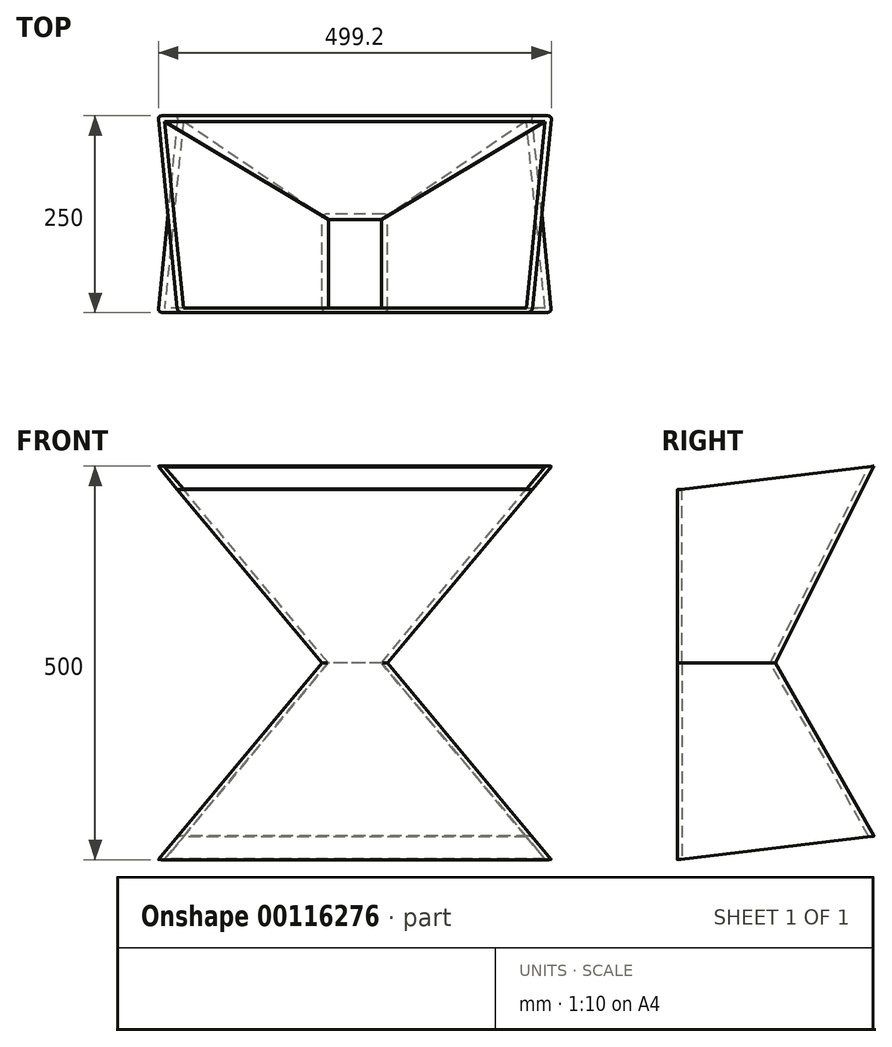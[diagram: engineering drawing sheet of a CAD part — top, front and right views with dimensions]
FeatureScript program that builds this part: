
annotation { "Feature Type Name" : "Feature", "Feature Type Description" : "" }
export const myFeature = defineFeature(function(context is Context, id is Id, definition is map)
    precondition{}
    {
        {
            var Q0;
            Q0=qCreatedBy(makeId("Front.planeOp"),FACE);
            var sketch = newSketch(context, id + "F0", { "sketchPlane" : qUnion([Q0])});
            skLineSegment(sketch, "E0.bottom", {"start": v(250, -250) * mm, "end": v(-250, -250) * mm});
            skLineSegment(sketch, "E0.top", {"start": v(250, 250) * mm, "end": v(-250, 250) * mm});
            skPoint(sketch, "E0.middle", {"position": v(0, 0) * mm});
            skLineSegment(sketch, "E1", {"start": v(-41.48, 0) * mm, "end": v(-250, 250) * mm});
            skLineSegment(sketch, "E2.MirrorCS", {"start": v(41.48, 0) * mm, "end": v(250, 250) * mm});
            skPoint(sketch, "E3.MirrorCS.end.orphan", {"position": v(41.48, 0) * mm});
            skLineSegment(sketch, "E4", {"start": v(-41.48, 0) * mm, "end": v(-250, -250) * mm});
            skLineSegment(sketch, "E5", {"start": v(41.48, 0) * mm, "end": v(250, -250) * mm});
            skSolve(sketch);
        }
        {
            var Q0;
            Q0 = qSketchRegion(id + "F0", true);
            extrude(context, id + "F1", {"entities" : qUnion([Q0]), "endBound" : BoundingType.SYMMETRIC, "depth" : 250 * mm});
        }
        {
            var Q0;
            Q0=makeQuery(id+"F1.opExtrude","CAP_EDGE",EDGE,{"disambiguationData":[OSD([sQuery(id+"F0.wireOp",EDGE,"E0.bottom")])],"isStart":true});
            var Q1;
            Q1=makeQuery(id+"F1.opExtrude","CAP_EDGE",EDGE,{"disambiguationData":[OSD([sQuery(id+"F0.wireOp",EDGE,"E0.top")])],"isStart":false});
            chamfer(context, id + "F2", {"entities" : qUnion([Q0, Q1]), "chamferType" : ChamferType.TWO_OFFSETS, "width1" : 30 * mm, "oppositeDirection" : false, "width2" : 250 * mm, "tangentPropagation" : true});
        }
        {
            var Q0;
            Q0=qCreatedBy(makeId("Right.planeOp"),FACE);
            var sketch = newSketch(context, id + "F3", { "sketchPlane" : qUnion([Q0])});
            skLineSegment(sketch, "E6.0", {"start": v(125, 0) * mm, "end": v(125, -220) * mm});
            skLineSegment(sketch, "E7.0", {"start": v(125, 0) * mm, "end": v(125, 250) * mm});
            skLineSegment(sketch, "E8", {"start": v(0, 0) * mm, "end": v(125, -220) * mm});
            skLineSegment(sketch, "E9", {"start": v(0, 0) * mm, "end": v(125, 250) * mm});
            skPoint(sketch, "E10.0.end.orphan", {"position": v(-125, 220) * mm});
            skPoint(sketch, "E11.0.start.orphan", {"position": v(-125, -250) * mm});
            skPoint(sketch, "E12.orphan", {"position": v(-125, 0) * mm});
            skSolve(sketch);
        }
        {
            var Q0;
            Q0 = qSketchRegion(id + "F3", true);
            extrude(context, id + "F4", {"entities" : qUnion([Q0]), "operationType" : NewBodyOperationType.REMOVE, "endBound" : BoundingType.SYMMETRIC, "depth" : 500 * mm});
        }
        {
            var Q0;
            Q0=makeQuery(id+"F2.opChamfer","BLEND_FACE",FACE,{"disambiguationData":[OSD([sQuery(id+"F0.wireOp",EDGE,"E0.bottom")])]});
            var Q1;
            Q1=makeQuery(id+"F2.opChamfer","BLEND_FACE",FACE,{"disambiguationData":[OSD([sQuery(id+"F0.wireOp",EDGE,"E0.top")])]});
            shell(context, id + "F5", {"entities" : qUnion([Q0, Q1]), "thickness" : 6 * mm});
        }
        {
            var Q0;
            Q0=makeQuery(id+"F1.opExtrude","CAP_EDGE",EDGE,{"disambiguationData":[OSD([sQuery(id+"F0.wireOp",EDGE,"E1")])],"isStart":false});
            var Q1;
            Q1=makeQuery(id+"F1.opExtrude","CAP_EDGE",EDGE,{"disambiguationData":[OSD([sQuery(id+"F0.wireOp",EDGE,"E2.MirrorCS")])],"isStart":false});
            var Q2;
            Q2=makeQuery(id+"F4.boolean.opBoolean","INTERSECT",EDGE,{"derivedFrom":[makeQuery(id+"F1.opExtrude","SWEPT_FACE",FACE,{"disambiguationData":[OSD([sQuery(id+"F0.wireOp",EDGE,"E2.MirrorCS")])]}),makeQuery(id+"F4.opExtrude","SWEPT_FACE",FACE,{"disambiguationData":[OSD([sQuery(id+"F3.wireOp",EDGE,"E9")])]})]});
            var Q3;
            Q3=makeQuery(id+"F4.boolean.opBoolean","INTERSECT",EDGE,{"derivedFrom":[makeQuery(id+"F1.opExtrude","SWEPT_FACE",FACE,{"disambiguationData":[OSD([sQuery(id+"F0.wireOp",EDGE,"E5")])]}),makeQuery(id+"F4.opExtrude","SWEPT_FACE",FACE,{"disambiguationData":[OSD([sQuery(id+"F3.wireOp",EDGE,"E8")])]})]});
            var Q4;
            Q4=makeQuery(id+"F1.opExtrude","CAP_EDGE",EDGE,{"disambiguationData":[OSD([sQuery(id+"F0.wireOp",EDGE,"E5")])],"isStart":false});
            var Q5;
            Q5=makeQuery(id+"F1.opExtrude","CAP_EDGE",EDGE,{"disambiguationData":[OSD([sQuery(id+"F0.wireOp",EDGE,"E4")])],"isStart":false});
            var Q6;
            Q6=makeQuery(id+"F4.boolean.opBoolean","INTERSECT",EDGE,{"derivedFrom":[makeQuery(id+"F1.opExtrude","SWEPT_FACE",FACE,{"disambiguationData":[OSD([sQuery(id+"F0.wireOp",EDGE,"E4")])]}),makeQuery(id+"F4.opExtrude","SWEPT_FACE",FACE,{"disambiguationData":[OSD([sQuery(id+"F3.wireOp",EDGE,"E8")])]})]});
            var Q7;
            Q7=makeQuery(id+"F4.boolean.opBoolean","INTERSECT",EDGE,{"derivedFrom":[makeQuery(id+"F1.opExtrude","SWEPT_FACE",FACE,{"disambiguationData":[OSD([sQuery(id+"F0.wireOp",EDGE,"E1")])]}),makeQuery(id+"F4.opExtrude","SWEPT_FACE",FACE,{"disambiguationData":[OSD([sQuery(id+"F3.wireOp",EDGE,"E9")])]})]});
            fillet(context, id + "F6", {"entities" : qUnion([Q0, Q1, Q2, Q3, Q4, Q5, Q6, Q7]), "radius" : 5 * mm, "tangentPropagation" : true, "allowEdgeOverflow" : false});
        }
    });
